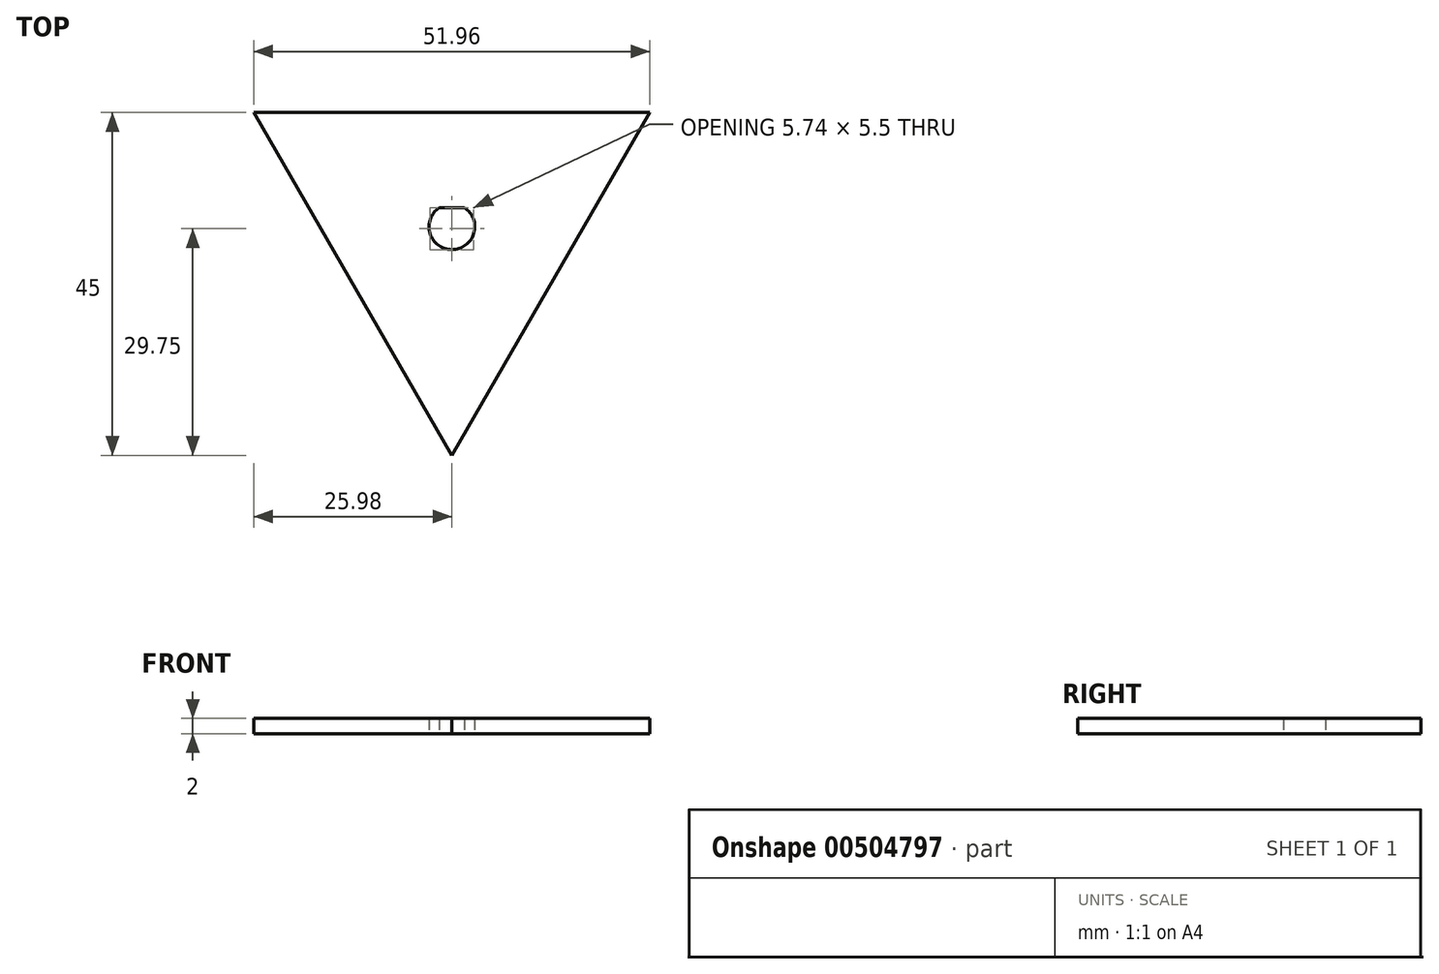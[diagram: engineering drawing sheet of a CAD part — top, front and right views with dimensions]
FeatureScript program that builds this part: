
annotation { "Feature Type Name" : "Feature", "Feature Type Description" : "" }
export const myFeature = defineFeature(function(context is Context, id is Id, definition is map)
    precondition{}
    {
        {
            var Q0;
            Q0=qCreatedBy(makeId("Top.planeOp"),FACE);
            var sketch = newSketch(context, id + "F0", { "sketchPlane" : qUnion([Q0])});
            skCircle(sketch, "E0.cCircle", {"center": v(0, 0) * mm, "radius": 15 * mm, "construction": true});
            skLineSegment(sketch, "E0.0", {"start": v(-25.98, 15) * mm, "end": v(25.98, 15) * mm});
            skLineSegment(sketch, "E0.1", {"start": v(25.98, 15) * mm, "end": v(0, -30) * mm});
            skLineSegment(sketch, "E0.2", {"start": v(0, -30) * mm, "end": v(-25.98, 15) * mm});
            skPoint(sketch, "E0.0.midPoint", {"position": v(0, 15) * mm});
            skCircle(sketch, "E1", {"center": v(0, 0) * mm, "radius": 3 * mm});
            skLineSegment(sketch, "E2", {"start": v(-1.66, 2.5) * mm, "end": v(1.66, 2.5) * mm});
            skSolve(sketch);
        }
        {
            var Q0;
            Q0 = qSketchRegion(id + "F0", true);
            var Q1;
            {var subQ0=sQuery(id+"F0.wireOp",EDGE,"E2");Q1=makeQuery(id+"F0.imprint","IMPRINT",FACE,{"disambiguationData":[TD([[makeQuery(id+"F0.imprint","IMPRINT",EDGE,{"derivedFrom":subQ0}),1.0]])]});}
            extrude(context, id + "F1", {"entities" : qUnion([Q0, Q1]), "depth" : 2 * mm});
        }
    });
